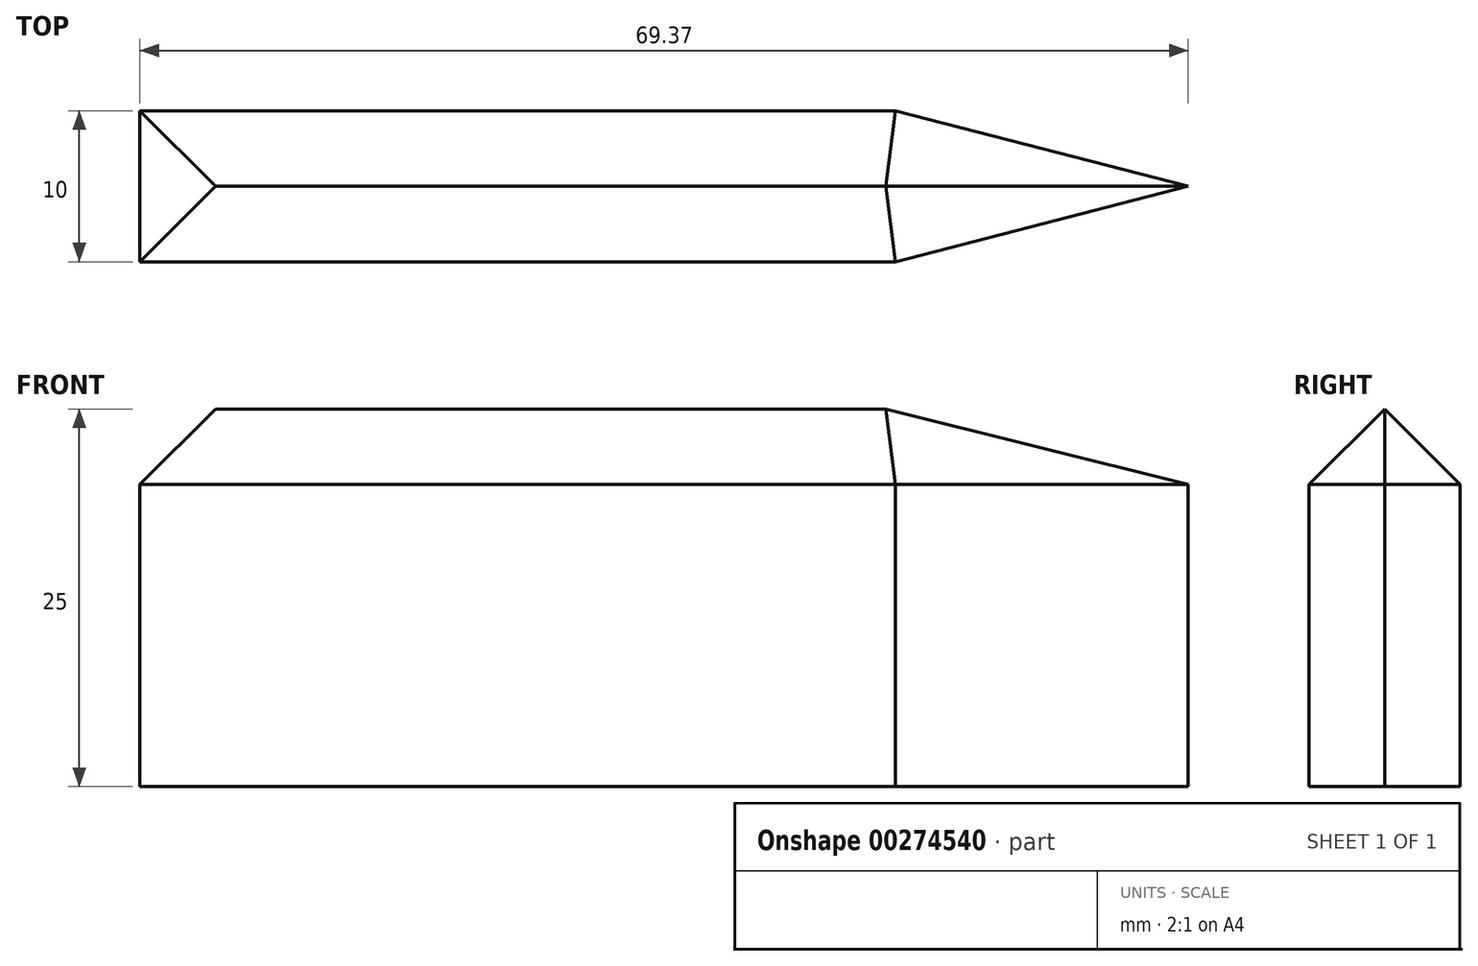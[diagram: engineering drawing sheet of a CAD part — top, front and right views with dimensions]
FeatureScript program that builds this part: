
annotation { "Feature Type Name" : "Feature", "Feature Type Description" : "" }
export const myFeature = defineFeature(function(context is Context, id is Id, definition is map)
    precondition{}
    {
        {
            var Q0;
            Q0=qCreatedBy(makeId("Top.planeOp"),FACE);
            var sketch = newSketch(context, id + "F0", { "sketchPlane" : qUnion([Q0])});
            skLineSegment(sketch, "E0.bottom", {"start": v(-49.57, -5) * mm, "end": v(0.43, -5) * mm});
            skLineSegment(sketch, "E0.top", {"start": v(-49.57, 5) * mm, "end": v(0.43, 5) * mm});
            skLineSegment(sketch, "E0.left", {"start": v(-49.57, -5) * mm, "end": v(-49.57, 5) * mm});
            skLineSegment(sketch, "E0.right", {"start": v(0.43, -5) * mm, "end": v(0.43, 5) * mm});
            skLineSegment(sketch, "E1", {"start": v(19.8, 0) * mm, "end": v(0.43, 5) * mm});
            skLineSegment(sketch, "E2", {"start": v(0.43, -5) * mm, "end": v(19.8, 0) * mm});
            skSolve(sketch);
        }
        {
            var Q0;
            Q0=makeQuery(id+"F0.imprint","IMPRINT",FACE,{"disambiguationData":[TD([[makeQuery(id+"F0.imprint","IMPRINT",EDGE,{"derivedFrom":sQuery(id+"F0.wireOp",EDGE,"E0.bottom")}),1.0]])]});
            var Q1;
            Q1=makeQuery(id+"F0.imprint","IMPRINT",FACE,{"disambiguationData":[TD([[makeQuery(id+"F0.imprint","IMPRINT",EDGE,{"derivedFrom":sQuery(id+"F0.wireOp",EDGE,"E0.right")}),-1.0]])]});
            extrude(context, id + "F1", {"entities" : qUnion([Q0, Q1]), "depth" : 25 * mm});
        }
        {
            var Q0;
            Q0=makeQuery(id+"F1.opExtrude","CAP_EDGE",EDGE,{"disambiguationData":[OSD([sQuery(id+"F0.wireOp",EDGE,"E0.bottom")])],"isStart":false});
            var Q1;
            Q1=makeQuery(id+"F1.opExtrude","CAP_EDGE",EDGE,{"disambiguationData":[OSD([sQuery(id+"F0.wireOp",EDGE,"E0.left")])],"isStart":false});
            var Q2;
            Q2=makeQuery(id+"F1.opExtrude","CAP_EDGE",EDGE,{"disambiguationData":[OSD([sQuery(id+"F0.wireOp",EDGE,"E0.top")])],"isStart":false});
            var Q3;
            Q3=makeQuery(id+"F1.opExtrude","CAP_EDGE",EDGE,{"disambiguationData":[OSD([sQuery(id+"F0.wireOp",EDGE,"E1")])],"isStart":false});
            var Q4;
            Q4=makeQuery(id+"F1.opExtrude","CAP_EDGE",EDGE,{"disambiguationData":[OSD([sQuery(id+"F0.wireOp",EDGE,"E2")])],"isStart":false});
            chamfer(context, id + "F2", {"entities" : qUnion([Q0, Q1, Q2, Q3, Q4]), "width" : 5 * mm, "tangentPropagation" : true});
        }
    });
